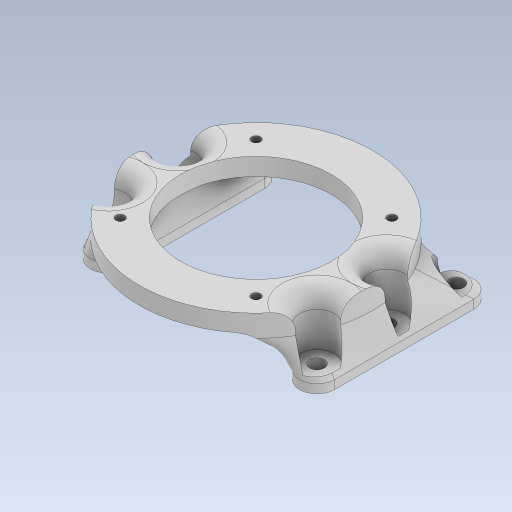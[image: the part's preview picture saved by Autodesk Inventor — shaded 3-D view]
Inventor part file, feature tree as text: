
AUTODESK INVENTOR PART (.ipt)
format: ipt  version: 2023 (Build 270158000, 158)  size: 505,856 bytes
history: native  units: in
note: dims shown in document units (in); Inventor stores cm internally (conversion verified against a paired STEP export)
features: sketch x4, other x4, extrude x3, projected_geometry x3, hole x2, loft x2, fillet x2, plane x1
ambient origin geometry x8: Origin, YZ Plane, XZ Plane, XY Plane, X Axis, Y Axis, Z Axis, Center Point
bodies: Solid1 (feature_tree)
feature tree (21):
  sketch  "Sketch1"  dims[d1=1.5748in d2=360.0deg d3=0.1575in d4=0.7232in d5=0.375in d6=0.375in d7=0.5in d8=0.2963in]
  extrude  "Extrusion1"  Depth=0.2963in
  hole  "Hole1"  [1 undecoded]
  plane  "Work Plane1"
  extrude  "Extrusion2"  Depth=0.125in
  extrude  "Extrusion6"  Depth=0.125in TaperAngle=360.0deg
  loft  "Loft1"
  loft  "Loft2"
  hole  "Hole2"  [1 undecoded]
  fillet  "Fillet4"  Radius=0.25in
  fillet  "Fillet5"  Radius=0.5in
  sketch  "Sketch2"  dims[d10=0.25in d11=0.0in]
  sketch  "Sketch7"  dims[d12=0.1276in d13=0.315in d14=0.1654in d15=0.125in d16=0.5635in d17=1.0in d18=0.8108in d19=-0.9471in]
  projected_geometry  "Projected Loop3"
  other  "Edges1"
  other  "Edges2"
  other  "Edges3"
  other  "Edges4"
  sketch  "Sketch8"  dims[d20=3.0in d21=2.0in d22=3.1496in d24=360.0deg d26=0.2087in d27=1.1811in d29=1.0in d30=0.7874in d32=3.0in d35=0.25in d36=0.25in d37=0.5in d38=0.25in d39=0.125in d40=0.0in d58=0.25in d63=0.0625in d64=0.0625in d65=0.0625in d66=0.0in d67=0.0in d68=90.0deg d69=0.0in d70=90.0deg d71=0.0in d72=90.0deg d73=0.0in d74=90.0deg d77=0.2087in d78=1.1811in d80=1.0in d81=0.7874in d83=3.0in d86=0.2126in d87=0.328in d88=0.5in d89=0.75in d90=0.5635in d91=1.0in d92=0.8108in d93=0.375in d94=0.25in d95=0.125in d59=0.0in d60=0.0in d61=0.0in]
  projected_geometry  "Projected Loop4"
  projected_geometry  "Projected Loop5"
note: 2 required parameter values undecoded (feature->parameter linkage not recoverable at this tier; creation-order binding heuristic only, values carry confidence <= 0.55)
